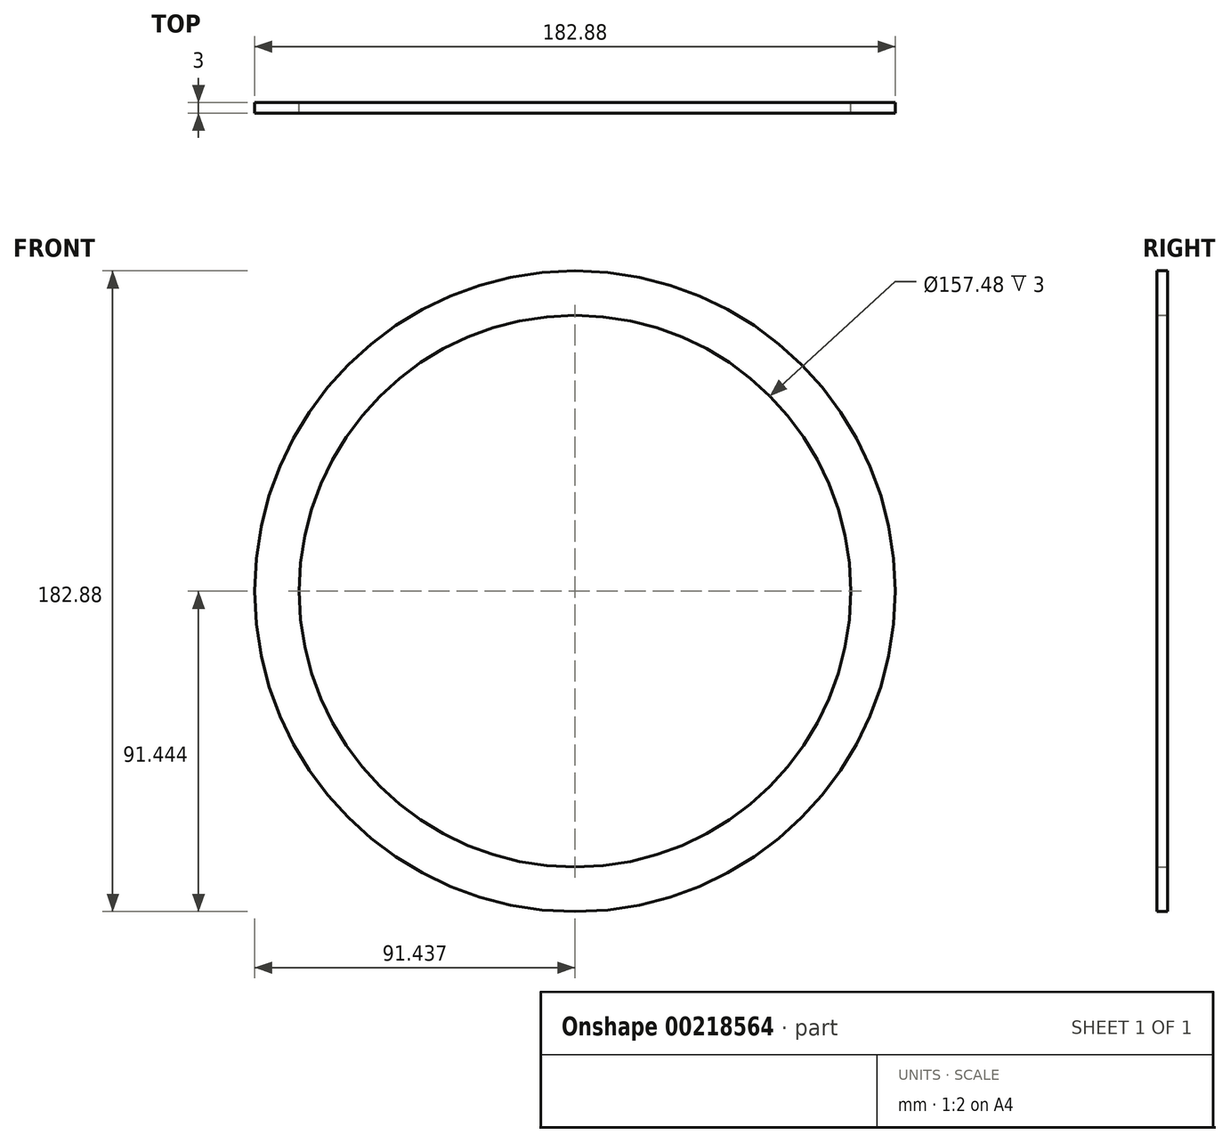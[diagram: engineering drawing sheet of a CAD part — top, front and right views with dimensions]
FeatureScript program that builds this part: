
annotation { "Feature Type Name" : "Feature", "Feature Type Description" : "" }
export const myFeature = defineFeature(function(context is Context, id is Id, definition is map)
    precondition{}
    {
        {
            var Q0;
            Q0=qCreatedBy(makeId("Front.planeOp"),FACE);
            var sketch = newSketch(context, id + "F0", { "sketchPlane" : qUnion([Q0])});
            skCircle(sketch, "E0", {"center": v(-18.1, 4.9) * mm, "radius": 78.74 * mm});
            skCircle(sketch, "E1", {"center": v(-18.1, 4.9) * mm, "radius": 91.44 * mm});
            skSolve(sketch);
        }
        {
            var Q0;
            Q0=makeQuery(id+"F0.imprint","IMPRINT",FACE,{"disambiguationData":[TD([[makeQuery(id+"F0.imprint","IMPRINT",EDGE,{"derivedFrom":sQuery(id+"F0.wireOp",EDGE,"E0")}),-1.0]])]});
            extrude(context, id + "F1", {"entities" : qUnion([Q0]), "depth" : 3 * mm});
        }
    });
